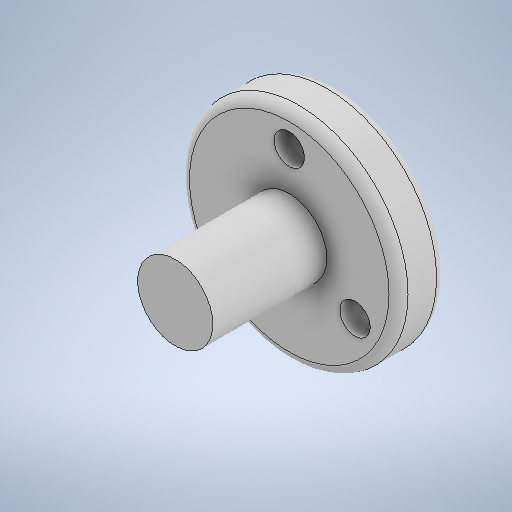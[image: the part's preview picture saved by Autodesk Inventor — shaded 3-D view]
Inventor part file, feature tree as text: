
AUTODESK INVENTOR PART (.ipt)
format: ipt  version: 2025.2 (Build 292293000, 293)  size: 278,016 bytes
history: native  units: in
note: dims shown in document units (in); Inventor stores cm internally (conversion verified against a paired STEP export)
features: sketch x4, extrude x2, hole x1, fillet x1
ambient origin geometry x8: Origin, YZ Plane, XZ Plane, XY Plane, X Axis, Y Axis, Z Axis, Center Point
bodies: Solid1 (feature_tree)
feature tree (8):
  extrude  "Extrusion1"  Depth=0.1969in TaperAngle=0.0deg
  extrude  "Extrusion2"  Depth=0.4724in TaperAngle=0.0deg
  hole  "Hole1"  [1 undecoded]
  fillet  "Fillet1"  Radius=0.0394in
  sketch  "Sketch1"  dims[d0=0.9055in d1=0.1969in d2=0.0in]
  sketch  "Sketch2"  dims[d6=1.1811in d8=360.0deg]
  sketch  "Sketch3"  dims[d10=0.126in d11=0.2362in d12=0.1575in d13=0.0787in d14=90.0deg d15=0.315in d16=0.8108in d17=0.315in d18=0.0394in]
  sketch  "Sketch Circular Pattern1"  dims[d3=0.311in d4=0.4724in d5=0.0in]
note: 1 required parameter value undecoded (feature->parameter linkage not recoverable at this tier; creation-order binding heuristic only, values carry confidence <= 0.55)
